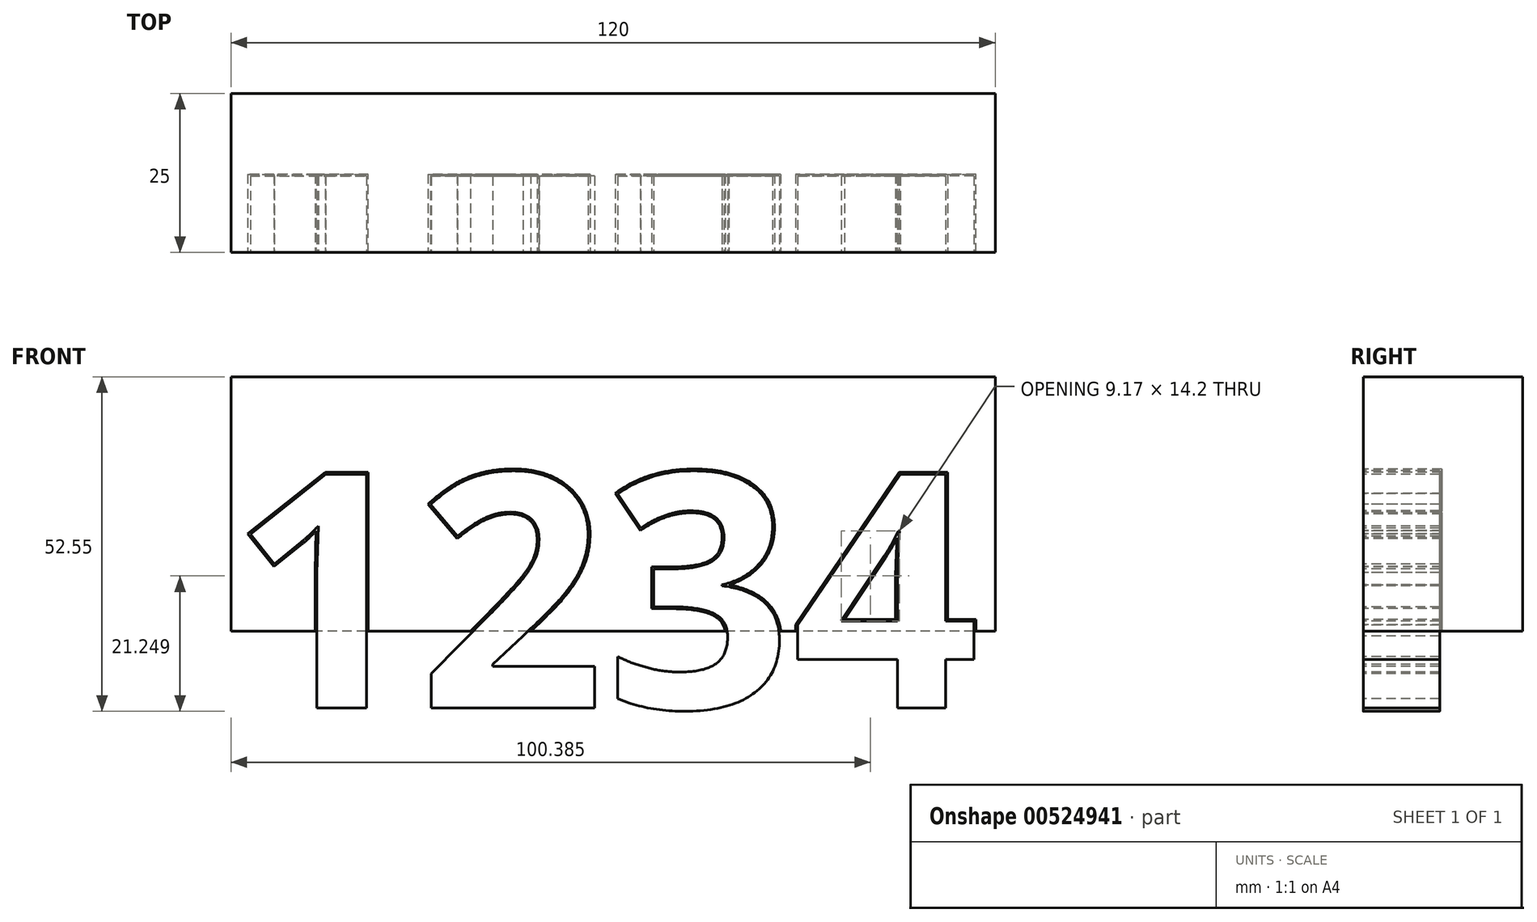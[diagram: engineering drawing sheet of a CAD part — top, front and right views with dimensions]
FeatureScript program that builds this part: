
annotation { "Feature Type Name" : "Feature", "Feature Type Description" : "" }
export const myFeature = defineFeature(function(context is Context, id is Id, definition is map)
    precondition{}
    {
        {
            var Q0;
            Q0=qCreatedBy(makeId("Front.planeOp"),FACE);
            var sketch = newSketch(context, id + "F0", { "sketchPlane" : qUnion([Q0])});
            skLineSegment(sketch, "E0.bottom", {"start": v(0, 0) * mm, "end": v(120, 0) * mm});
            skLineSegment(sketch, "E0.top", {"start": v(0, 40) * mm, "end": v(120, 40) * mm});
            skLineSegment(sketch, "E0.left", {"start": v(0, 0) * mm, "end": v(0, 40) * mm});
            skLineSegment(sketch, "E0.right", {"start": v(120, 0) * mm, "end": v(120, 40) * mm});
            skSolve(sketch);
        }
        {
            var Q0;
            Q0=makeQuery(id+"F0.imprint","IMPRINT",FACE,{"disambiguationData":[TD([[makeQuery(id+"F0.imprint","IMPRINT",EDGE,{"derivedFrom":sQuery(id+"F0.wireOp",EDGE,"E0.bottom")}),1.0]])]});
            var sketch = newSketch(context, id + "F1", { "sketchPlane" : qUnion([Q0])});
            skText(sketch, "E1", { "text": "1234", "fontName": "OpenSans-Bold.ttf"});
            const initialGuessF1  = {"E1": [0, -0.03704, 1, 0, 0.03704]};
            skSetInitialGuess(sketch, initialGuessF1);
            skSolve(sketch);
        }
        {
            var Q0;
            Q0=makeQuery(id+"F0.imprint","IMPRINT",FACE,{"disambiguationData":[TD([[makeQuery(id+"F0.imprint","IMPRINT",EDGE,{"derivedFrom":sQuery(id+"F0.wireOp",EDGE,"E0.bottom")}),1.0]])]});
            extrude(context, id + "F2", {"entities" : qUnion([Q0]), "oppositeDirection" : true, "depth" : 25 * mm, "offsetDistance" : 25 * mm});
        }
        {
            var Q0;
            Q0 = qSketchRegion(id + "F1", true);
            extrude(context, id + "F3", {"entities" : qUnion([Q0]), "oppositeDirection" : true, "depth" : 12 * mm, "offsetDistance" : 25 * mm});
        }
        {
            var Q0;
            Q0=makeQuery(id+"F3.opExtrude","SWEPT_BODY",BODY,{"disambiguationData":[OSD([sQuery(id+"F1.wireOp",EDGE,"E1.sketch_text.stroke-61"),sQuery(id+"F1.wireOp",EDGE,"E1.sketch_text.stroke-62"),sQuery(id+"F1.wireOp",EDGE,"E1.sketch_text.stroke-63"),sQuery(id+"F1.wireOp",EDGE,"E1.sketch_text.stroke-64"),sQuery(id+"F1.wireOp",EDGE,"E1.sketch_text.stroke-65"),sQuery(id+"F1.wireOp",EDGE,"E1.sketch_text.stroke-66"),sQuery(id+"F1.wireOp",EDGE,"E1.sketch_text.stroke-67"),sQuery(id+"F1.wireOp",EDGE,"E1.sketch_text.stroke-68"),sQuery(id+"F1.wireOp",EDGE,"E1.sketch_text.stroke-69"),sQuery(id+"F1.wireOp",EDGE,"E1.sketch_text.stroke-70"),sQuery(id+"F1.wireOp",EDGE,"E1.sketch_text.stroke-71"),sQuery(id+"F1.wireOp",EDGE,"E1.sketch_text.stroke-72"),sQuery(id+"F1.wireOp",EDGE,"E1.sketch_text.stroke-73"),sQuery(id+"F1.wireOp",EDGE,"E1.sketch_text.stroke-74"),sQuery(id+"F1.wireOp",EDGE,"E1.sketch_text.stroke-75"),sQuery(id+"F1.wireOp",EDGE,"E1.sketch_text.stroke-76"),sQuery(id+"F1.wireOp",EDGE,"E1.sketch_text.stroke-77"),sQuery(id+"F1.wireOp",EDGE,"E1.sketch_text.stroke-78")])]});
            var Q1;
            Q1=makeQuery(id+"F3.opExtrude","SWEPT_BODY",BODY,{"disambiguationData":[OSD([sQuery(id+"F1.wireOp",EDGE,"E1.sketch_text.stroke-34"),sQuery(id+"F1.wireOp",EDGE,"E1.sketch_text.stroke-35"),sQuery(id+"F1.wireOp",EDGE,"E1.sketch_text.stroke-36"),sQuery(id+"F1.wireOp",EDGE,"E1.sketch_text.stroke-37"),sQuery(id+"F1.wireOp",EDGE,"E1.sketch_text.stroke-38"),sQuery(id+"F1.wireOp",EDGE,"E1.sketch_text.stroke-39"),sQuery(id+"F1.wireOp",EDGE,"E1.sketch_text.stroke-40"),sQuery(id+"F1.wireOp",EDGE,"E1.sketch_text.stroke-41"),sQuery(id+"F1.wireOp",EDGE,"E1.sketch_text.stroke-42"),sQuery(id+"F1.wireOp",EDGE,"E1.sketch_text.stroke-43"),sQuery(id+"F1.wireOp",EDGE,"E1.sketch_text.stroke-44"),sQuery(id+"F1.wireOp",EDGE,"E1.sketch_text.stroke-45"),sQuery(id+"F1.wireOp",EDGE,"E1.sketch_text.stroke-46"),sQuery(id+"F1.wireOp",EDGE,"E1.sketch_text.stroke-47"),sQuery(id+"F1.wireOp",EDGE,"E1.sketch_text.stroke-48"),sQuery(id+"F1.wireOp",EDGE,"E1.sketch_text.stroke-49"),sQuery(id+"F1.wireOp",EDGE,"E1.sketch_text.stroke-50"),sQuery(id+"F1.wireOp",EDGE,"E1.sketch_text.stroke-51"),sQuery(id+"F1.wireOp",EDGE,"E1.sketch_text.stroke-52"),sQuery(id+"F1.wireOp",EDGE,"E1.sketch_text.stroke-53"),sQuery(id+"F1.wireOp",EDGE,"E1.sketch_text.stroke-54"),sQuery(id+"F1.wireOp",EDGE,"E1.sketch_text.stroke-55"),sQuery(id+"F1.wireOp",EDGE,"E1.sketch_text.stroke-56"),sQuery(id+"F1.wireOp",EDGE,"E1.sketch_text.stroke-57"),sQuery(id+"F1.wireOp",EDGE,"E1.sketch_text.stroke-58"),sQuery(id+"F1.wireOp",EDGE,"E1.sketch_text.stroke-59"),sQuery(id+"F1.wireOp",EDGE,"E1.sketch_text.stroke-60")])]});
            var Q2;
            Q2=makeQuery(id+"F3.opExtrude","SWEPT_BODY",BODY,{"disambiguationData":[OSD([sQuery(id+"F1.wireOp",EDGE,"E1.sketch_text.stroke-0"),sQuery(id+"F1.wireOp",EDGE,"E1.sketch_text.stroke-1"),sQuery(id+"F1.wireOp",EDGE,"E1.sketch_text.stroke-2"),sQuery(id+"F1.wireOp",EDGE,"E1.sketch_text.stroke-3"),sQuery(id+"F1.wireOp",EDGE,"E1.sketch_text.stroke-4"),sQuery(id+"F1.wireOp",EDGE,"E1.sketch_text.stroke-5"),sQuery(id+"F1.wireOp",EDGE,"E1.sketch_text.stroke-6"),sQuery(id+"F1.wireOp",EDGE,"E1.sketch_text.stroke-7"),sQuery(id+"F1.wireOp",EDGE,"E1.sketch_text.stroke-8"),sQuery(id+"F1.wireOp",EDGE,"E1.sketch_text.stroke-9")])]});
            var Q3;
            Q3=makeQuery(id+"F3.opExtrude","SWEPT_BODY",BODY,{"disambiguationData":[OSD([sQuery(id+"F1.wireOp",EDGE,"E1.sketch_text.stroke-10"),sQuery(id+"F1.wireOp",EDGE,"E1.sketch_text.stroke-11"),sQuery(id+"F1.wireOp",EDGE,"E1.sketch_text.stroke-12"),sQuery(id+"F1.wireOp",EDGE,"E1.sketch_text.stroke-13"),sQuery(id+"F1.wireOp",EDGE,"E1.sketch_text.stroke-14"),sQuery(id+"F1.wireOp",EDGE,"E1.sketch_text.stroke-15"),sQuery(id+"F1.wireOp",EDGE,"E1.sketch_text.stroke-16"),sQuery(id+"F1.wireOp",EDGE,"E1.sketch_text.stroke-17"),sQuery(id+"F1.wireOp",EDGE,"E1.sketch_text.stroke-18"),sQuery(id+"F1.wireOp",EDGE,"E1.sketch_text.stroke-19"),sQuery(id+"F1.wireOp",EDGE,"E1.sketch_text.stroke-20"),sQuery(id+"F1.wireOp",EDGE,"E1.sketch_text.stroke-21"),sQuery(id+"F1.wireOp",EDGE,"E1.sketch_text.stroke-22"),sQuery(id+"F1.wireOp",EDGE,"E1.sketch_text.stroke-23"),sQuery(id+"F1.wireOp",EDGE,"E1.sketch_text.stroke-24"),sQuery(id+"F1.wireOp",EDGE,"E1.sketch_text.stroke-25"),sQuery(id+"F1.wireOp",EDGE,"E1.sketch_text.stroke-26"),sQuery(id+"F1.wireOp",EDGE,"E1.sketch_text.stroke-27"),sQuery(id+"F1.wireOp",EDGE,"E1.sketch_text.stroke-28"),sQuery(id+"F1.wireOp",EDGE,"E1.sketch_text.stroke-29"),sQuery(id+"F1.wireOp",EDGE,"E1.sketch_text.stroke-30"),sQuery(id+"F1.wireOp",EDGE,"E1.sketch_text.stroke-31"),sQuery(id+"F1.wireOp",EDGE,"E1.sketch_text.stroke-32"),sQuery(id+"F1.wireOp",EDGE,"E1.sketch_text.stroke-33")])]});
            transform(context, id + "F4", {"entities" : qUnion([Q0, Q1, Q2, Q3]), "transformType" : TransformType.TRANSLATION_3D, "dx" : 0 * mm, "dy" : 0 * mm, "dz" : 25 * mm, "makeCopy" : false});
        }
        {
            var Q0;
            Q0=makeQuery(id+"F3.opExtrude","SWEPT_BODY",BODY,{"disambiguationData":[OSD([sQuery(id+"F1.wireOp",EDGE,"E1.sketch_text.stroke-0"),sQuery(id+"F1.wireOp",EDGE,"E1.sketch_text.stroke-1"),sQuery(id+"F1.wireOp",EDGE,"E1.sketch_text.stroke-2"),sQuery(id+"F1.wireOp",EDGE,"E1.sketch_text.stroke-3"),sQuery(id+"F1.wireOp",EDGE,"E1.sketch_text.stroke-4"),sQuery(id+"F1.wireOp",EDGE,"E1.sketch_text.stroke-5"),sQuery(id+"F1.wireOp",EDGE,"E1.sketch_text.stroke-6"),sQuery(id+"F1.wireOp",EDGE,"E1.sketch_text.stroke-7"),sQuery(id+"F1.wireOp",EDGE,"E1.sketch_text.stroke-8"),sQuery(id+"F1.wireOp",EDGE,"E1.sketch_text.stroke-9")])]});
            var Q1;
            Q1=makeQuery(id+"F3.opExtrude","SWEPT_BODY",BODY,{"disambiguationData":[OSD([sQuery(id+"F1.wireOp",EDGE,"E1.sketch_text.stroke-10"),sQuery(id+"F1.wireOp",EDGE,"E1.sketch_text.stroke-11"),sQuery(id+"F1.wireOp",EDGE,"E1.sketch_text.stroke-12"),sQuery(id+"F1.wireOp",EDGE,"E1.sketch_text.stroke-13"),sQuery(id+"F1.wireOp",EDGE,"E1.sketch_text.stroke-14"),sQuery(id+"F1.wireOp",EDGE,"E1.sketch_text.stroke-15"),sQuery(id+"F1.wireOp",EDGE,"E1.sketch_text.stroke-16"),sQuery(id+"F1.wireOp",EDGE,"E1.sketch_text.stroke-17"),sQuery(id+"F1.wireOp",EDGE,"E1.sketch_text.stroke-18"),sQuery(id+"F1.wireOp",EDGE,"E1.sketch_text.stroke-19"),sQuery(id+"F1.wireOp",EDGE,"E1.sketch_text.stroke-20"),sQuery(id+"F1.wireOp",EDGE,"E1.sketch_text.stroke-21"),sQuery(id+"F1.wireOp",EDGE,"E1.sketch_text.stroke-22"),sQuery(id+"F1.wireOp",EDGE,"E1.sketch_text.stroke-23"),sQuery(id+"F1.wireOp",EDGE,"E1.sketch_text.stroke-24"),sQuery(id+"F1.wireOp",EDGE,"E1.sketch_text.stroke-25"),sQuery(id+"F1.wireOp",EDGE,"E1.sketch_text.stroke-26"),sQuery(id+"F1.wireOp",EDGE,"E1.sketch_text.stroke-27"),sQuery(id+"F1.wireOp",EDGE,"E1.sketch_text.stroke-28"),sQuery(id+"F1.wireOp",EDGE,"E1.sketch_text.stroke-29"),sQuery(id+"F1.wireOp",EDGE,"E1.sketch_text.stroke-30"),sQuery(id+"F1.wireOp",EDGE,"E1.sketch_text.stroke-31"),sQuery(id+"F1.wireOp",EDGE,"E1.sketch_text.stroke-32"),sQuery(id+"F1.wireOp",EDGE,"E1.sketch_text.stroke-33")])]});
            var Q2;
            Q2=makeQuery(id+"F3.opExtrude","SWEPT_BODY",BODY,{"disambiguationData":[OSD([sQuery(id+"F1.wireOp",EDGE,"E1.sketch_text.stroke-34"),sQuery(id+"F1.wireOp",EDGE,"E1.sketch_text.stroke-35"),sQuery(id+"F1.wireOp",EDGE,"E1.sketch_text.stroke-36"),sQuery(id+"F1.wireOp",EDGE,"E1.sketch_text.stroke-37"),sQuery(id+"F1.wireOp",EDGE,"E1.sketch_text.stroke-38"),sQuery(id+"F1.wireOp",EDGE,"E1.sketch_text.stroke-39"),sQuery(id+"F1.wireOp",EDGE,"E1.sketch_text.stroke-40"),sQuery(id+"F1.wireOp",EDGE,"E1.sketch_text.stroke-41"),sQuery(id+"F1.wireOp",EDGE,"E1.sketch_text.stroke-42"),sQuery(id+"F1.wireOp",EDGE,"E1.sketch_text.stroke-43"),sQuery(id+"F1.wireOp",EDGE,"E1.sketch_text.stroke-44"),sQuery(id+"F1.wireOp",EDGE,"E1.sketch_text.stroke-45"),sQuery(id+"F1.wireOp",EDGE,"E1.sketch_text.stroke-46"),sQuery(id+"F1.wireOp",EDGE,"E1.sketch_text.stroke-47"),sQuery(id+"F1.wireOp",EDGE,"E1.sketch_text.stroke-48"),sQuery(id+"F1.wireOp",EDGE,"E1.sketch_text.stroke-49"),sQuery(id+"F1.wireOp",EDGE,"E1.sketch_text.stroke-50"),sQuery(id+"F1.wireOp",EDGE,"E1.sketch_text.stroke-51"),sQuery(id+"F1.wireOp",EDGE,"E1.sketch_text.stroke-52"),sQuery(id+"F1.wireOp",EDGE,"E1.sketch_text.stroke-53"),sQuery(id+"F1.wireOp",EDGE,"E1.sketch_text.stroke-54"),sQuery(id+"F1.wireOp",EDGE,"E1.sketch_text.stroke-55"),sQuery(id+"F1.wireOp",EDGE,"E1.sketch_text.stroke-56"),sQuery(id+"F1.wireOp",EDGE,"E1.sketch_text.stroke-57"),sQuery(id+"F1.wireOp",EDGE,"E1.sketch_text.stroke-58"),sQuery(id+"F1.wireOp",EDGE,"E1.sketch_text.stroke-59"),sQuery(id+"F1.wireOp",EDGE,"E1.sketch_text.stroke-60")])]});
            var Q3;
            Q3=makeQuery(id+"F3.opExtrude","SWEPT_BODY",BODY,{"disambiguationData":[OSD([sQuery(id+"F1.wireOp",EDGE,"E1.sketch_text.stroke-61"),sQuery(id+"F1.wireOp",EDGE,"E1.sketch_text.stroke-62"),sQuery(id+"F1.wireOp",EDGE,"E1.sketch_text.stroke-63"),sQuery(id+"F1.wireOp",EDGE,"E1.sketch_text.stroke-64"),sQuery(id+"F1.wireOp",EDGE,"E1.sketch_text.stroke-65"),sQuery(id+"F1.wireOp",EDGE,"E1.sketch_text.stroke-66"),sQuery(id+"F1.wireOp",EDGE,"E1.sketch_text.stroke-67"),sQuery(id+"F1.wireOp",EDGE,"E1.sketch_text.stroke-68"),sQuery(id+"F1.wireOp",EDGE,"E1.sketch_text.stroke-69"),sQuery(id+"F1.wireOp",EDGE,"E1.sketch_text.stroke-70"),sQuery(id+"F1.wireOp",EDGE,"E1.sketch_text.stroke-71"),sQuery(id+"F1.wireOp",EDGE,"E1.sketch_text.stroke-72"),sQuery(id+"F1.wireOp",EDGE,"E1.sketch_text.stroke-73"),sQuery(id+"F1.wireOp",EDGE,"E1.sketch_text.stroke-74"),sQuery(id+"F1.wireOp",EDGE,"E1.sketch_text.stroke-75"),sQuery(id+"F1.wireOp",EDGE,"E1.sketch_text.stroke-76"),sQuery(id+"F1.wireOp",EDGE,"E1.sketch_text.stroke-77"),sQuery(id+"F1.wireOp",EDGE,"E1.sketch_text.stroke-78")])]});
            var Q4;
            Q4=makeQuery(id+"F2.opExtrude","SWEPT_BODY",BODY,{"disambiguationData":[OSD([sQuery(id+"F0.wireOp",EDGE,"E0.bottom"),sQuery(id+"F0.wireOp",EDGE,"E0.top"),sQuery(id+"F0.wireOp",EDGE,"E0.left"),sQuery(id+"F0.wireOp",EDGE,"E0.right")])]});
            booleanBodies(context, id + "F5", {"operationType" : BooleanOperationType.SUBTRACTION, "tools" : qUnion([Q0, Q1, Q2, Q3]), "targets" : qUnion([Q4]), "offset" : true, "offsetAll" : true, "offsetDistance" : 0.3 * mm, "keepTools" : true});
        }
    });
